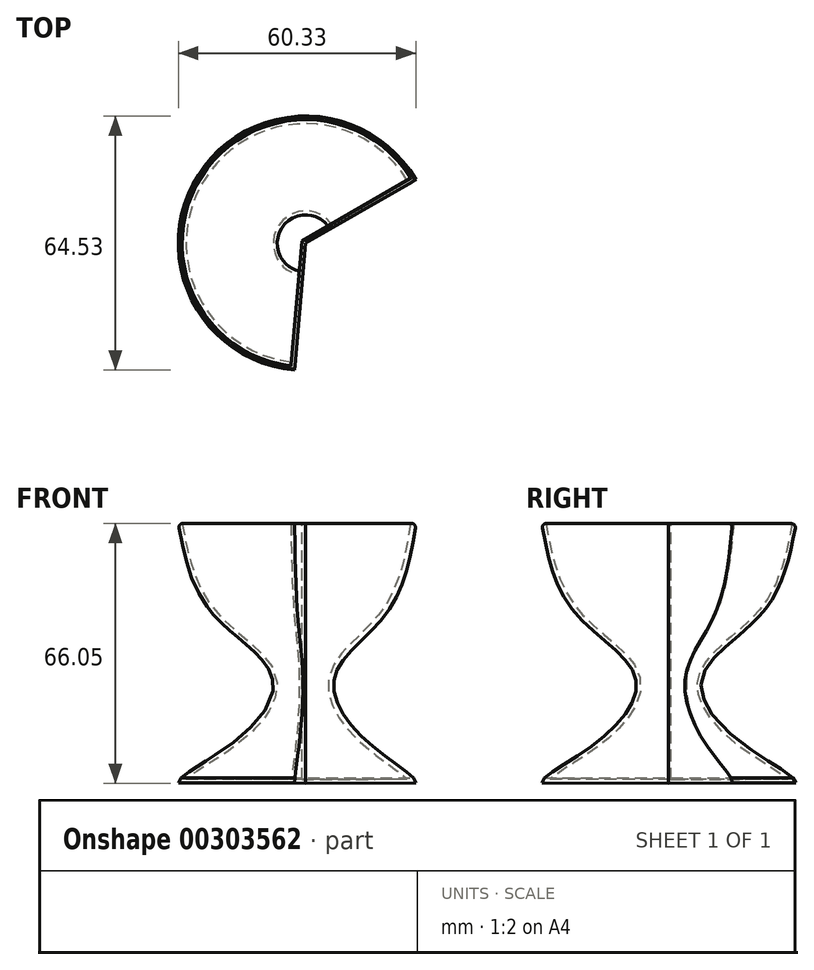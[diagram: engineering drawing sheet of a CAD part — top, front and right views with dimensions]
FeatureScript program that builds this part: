
annotation { "Feature Type Name" : "Feature", "Feature Type Description" : "" }
export const myFeature = defineFeature(function(context is Context, id is Id, definition is map)
    precondition{}
    {
        {
            var Q0;
            Q0=qCreatedBy(makeId("Front.planeOp"),FACE);
            var sketch = newSketch(context, id + "F0", { "sketchPlane" : qUnion([Q0])});
            skLineSegment(sketch, "E0", {"start": v(0, 0) * mm, "end": v(0, 66.05) * mm});
            skLineSegment(sketch, "E1", {"start": v(0, 66.05) * mm, "end": v(32.42, 66.05) * mm});
            skLineSegment(sketch, "E2", {"start": v(32.42, 0.16) * mm, "end": v(32.42, 0) * mm});
            skLineSegment(sketch, "E3", {"start": v(32.42, 0) * mm, "end": v(31.63, 1.36) * mm});
            skFitSpline(sketch, "E4", {"points": [v(32.42, 66.05) * mm, v(24.04, 43.62) * mm, v(8.57, 27.29) * mm, v(17.23, 11.32) * mm, v(32.42, 0) * mm, v(0, 0) * mm], "startDerivative": vector(-22.84, -118.06) * mm, "endDerivative": vector(-202.56, 16.23) * mm});
            skLineSegment(sketch, "E5", {"start": v(0, 0) * mm, "end": v(32.42, 0.16) * mm});
            skSolve(sketch);
        }
        {
            var Q0;
            {var subQ6=sQuery(id+"F0.wireOp",EDGE,"E0");Q0=makeQuery(id+"F0.imprint","IMPRINT",FACE,{"disambiguationData":[TD([[makeQuery(id+"F0.imprint","IMPRINT",EDGE,{"derivedFrom":subQ6}),-1.0]])]});}
            var Q1;
            Q1=sQuery(id+"F0.wireOp",EDGE,"E0");
            revolve(context, id + "F1", {"entities" : qUnion([Q0]), "axis" : qUnion([Q1]), "revolveType" : RevolveType.TWO_DIRECTIONS, "angle" : 265 * degree, "angleBack" : 30 * degree});
        }
        {
            var Q0;
            Q0=makeQuery(id+"F1.opRevolve","SWEPT_FACE",FACE,{"disambiguationData":[OSD([sQuery(id+"F0.wireOp",EDGE,"E1")])]});
            shell(context, id + "F2", {"entities" : qUnion([Q0]), "thickness" : 1 * mm});
        }
        {
            var Q0;
            Q0=makeQuery(id+"F1.opRevolve","SWEPT_EDGE",EDGE,{"disambiguationData":[OSD([sQuery(id+"F0.wireOp",EDGE,"E1"),sQuery(id+"F0.wireOp",EDGE,"E4")])]});
            fillet(context, id + "F3", {"entities" : qUnion([Q0]), "radius" : 1 * mm, "tangentPropagation" : true, "allowEdgeOverflow" : false});
        }
    });
